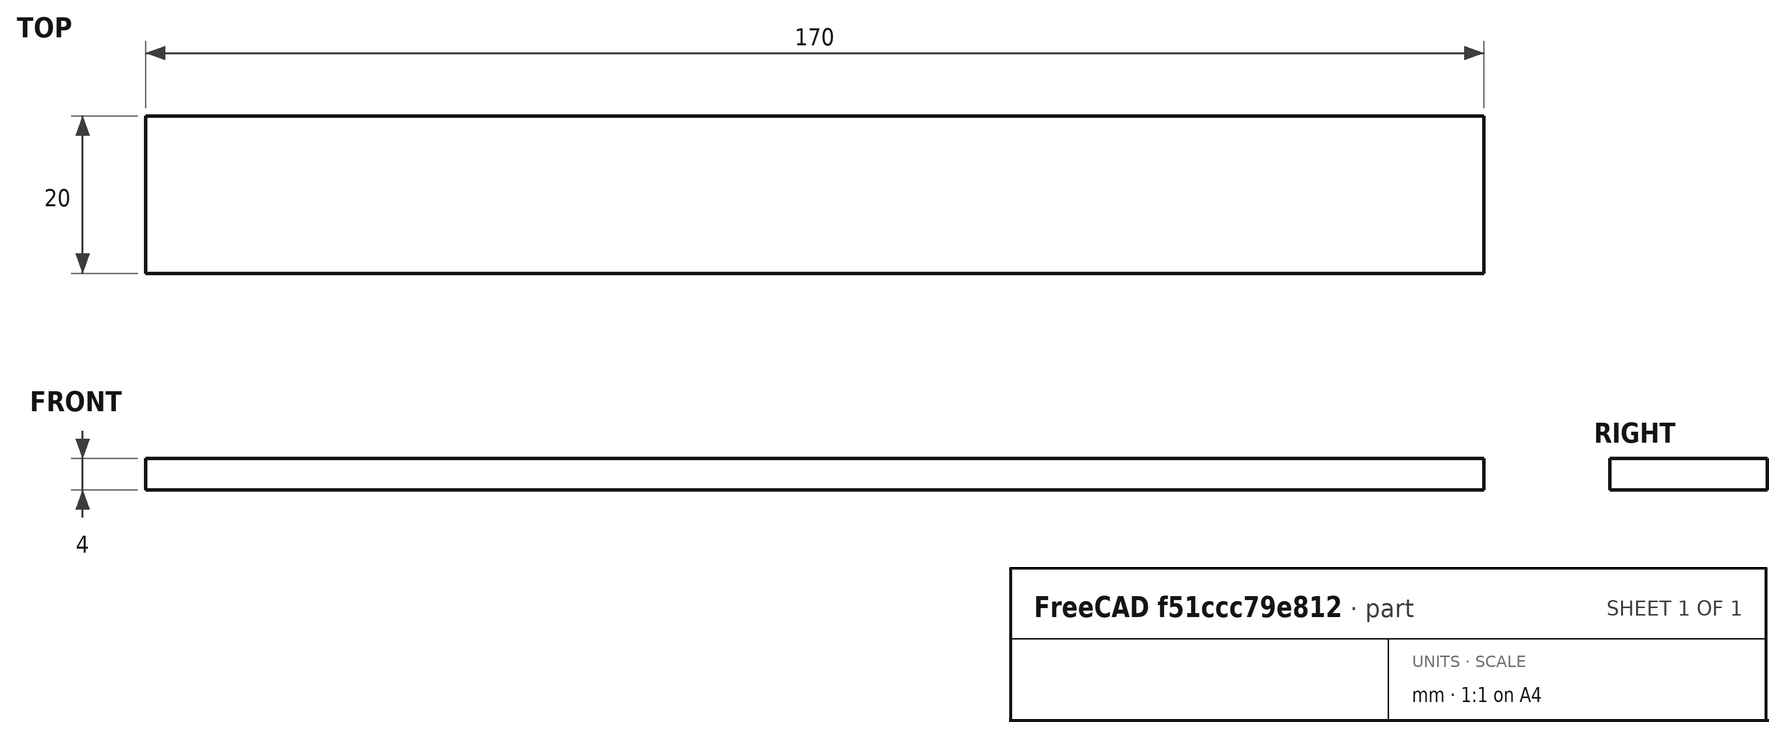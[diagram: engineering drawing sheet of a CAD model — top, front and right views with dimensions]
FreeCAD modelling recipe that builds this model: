
FCSTD DOCUMENT  (FreeCAD 0.17R13528 (Git))
Label: GlassDarkTop
License: All rights reserved
LicenseURL: http://en.wikipedia.org/wiki/All_rights_reserved
objects: Sketcher::SketchObject×1, PartDesign::Pad×1, PartDesign::Body×1
note: 4 computed .brp shape members not serialized (recipe doc carries the construction recipe); baked Part::Feature solids carry a one-line shape summary decoded from their .brp

FEATURE [Sketcher::SketchObject] Sketch
  MapMode = 5
  Support = -> [XY_Plane]
  sketch-geometry (4):
    g0: LineSegment StartX=0 StartY=0 StartZ=0 EndX=0 EndY=20 EndZ=0
    g1: LineSegment StartX=0 StartY=20 StartZ=0 EndX=170 EndY=20 EndZ=0
    g2: LineSegment StartX=170 StartY=20 StartZ=0 EndX=170 EndY=0 EndZ=0
    g3: LineSegment StartX=170 StartY=0 StartZ=0 EndX=0 EndY=0 EndZ=0
  constraints (11):
    c: Coincident(g0,g-1)
    c: Coincident(g1,g0)
    c: Horizontal(g1)
    c: Coincident(g2,g1)
    c: Coincident(g3,g2)
    c: Coincident(g3,g-1)
    c: Horizontal(g3)
    c: Vertical(g0)
    c: Vertical(g2)
    c: DistanceY(g0,g0) = 20
    c: DistanceX(g3,g3) = 170
FEATURE [PartDesign::Pad] Pad
  Length = 4
  Length2 = 100
  Profile = -> Sketch
  Type = 0
  expr: Length = Data#Spreadsheet.B1
FEATURE [PartDesign::Body] Body
  Group = -> [Sketch,Pad]
  Origin = -> Origin
  Tip = -> Pad
